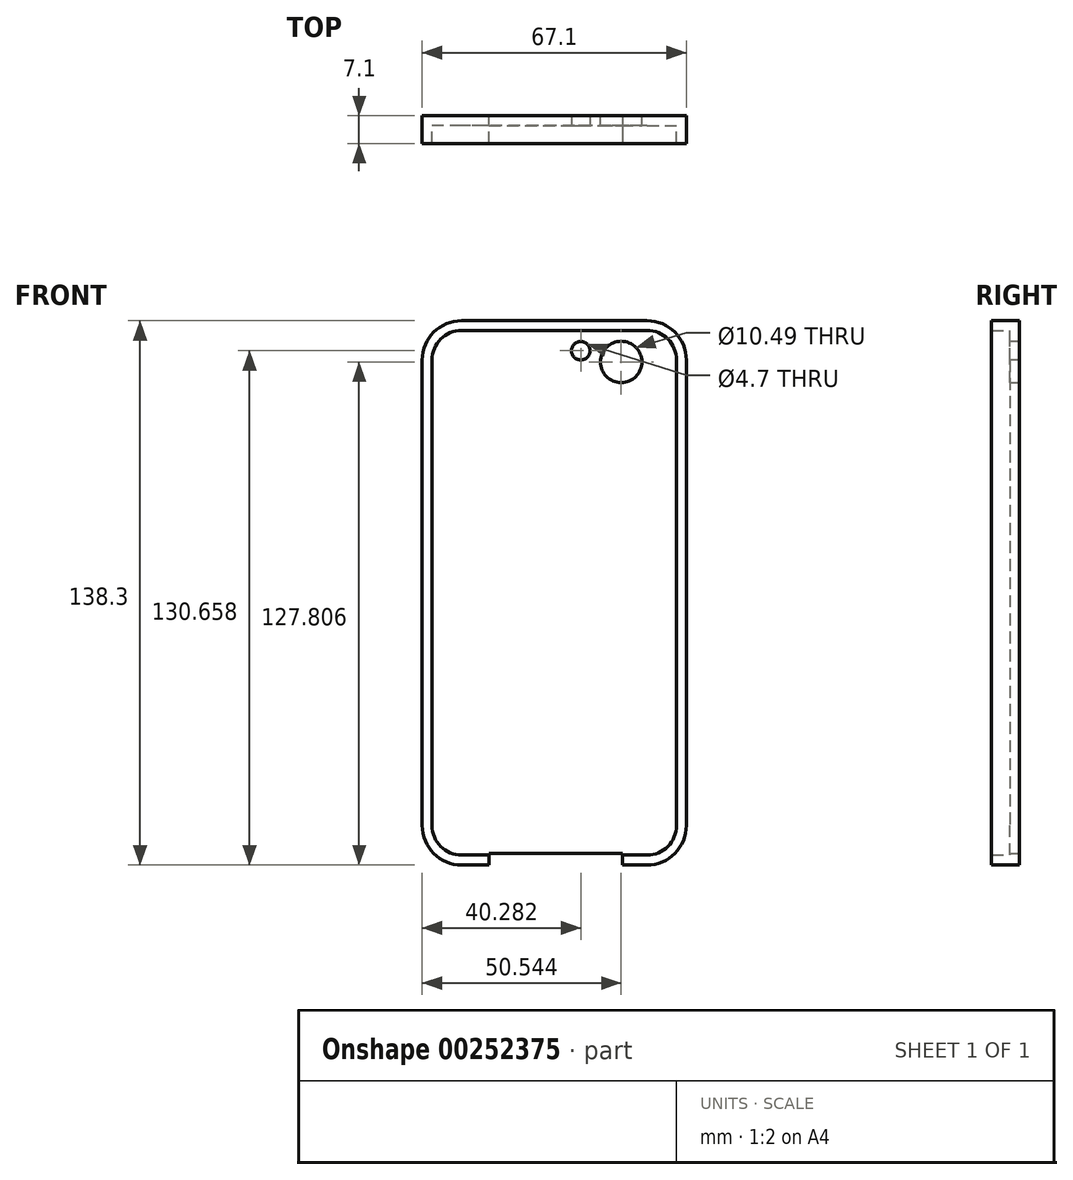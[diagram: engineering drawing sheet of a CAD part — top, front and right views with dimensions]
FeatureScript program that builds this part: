
annotation { "Feature Type Name" : "Feature", "Feature Type Description" : "" }
export const myFeature = defineFeature(function(context is Context, id is Id, definition is map)
    precondition{}
    {
        {
            var Q0;
            Q0=qCreatedBy(makeId("Front.planeOp"),FACE);
            var sketch = newSketch(context, id + "F0", { "sketchPlane" : qUnion([Q0])});
            skLineSegment(sketch, "E0.bottom", {"start": v(33.55, 69.15) * mm, "end": v(-33.55, 69.15) * mm});
            skLineSegment(sketch, "E0.top", {"start": v(33.55, -69.15) * mm, "end": v(-33.55, -69.15) * mm});
            skLineSegment(sketch, "E0.left", {"start": v(33.55, 69.15) * mm, "end": v(33.55, -69.15) * mm});
            skLineSegment(sketch, "E0.right", {"start": v(-33.55, 69.15) * mm, "end": v(-33.55, -69.15) * mm});
            skPoint(sketch, "E0.middle", {"position": v(0, 0) * mm});
            skSolve(sketch);
        }
        {
            var Q0;
            Q0=makeQuery(id+"F0.imprint","IMPRINT",FACE,{"disambiguationData":[TD([[makeQuery(id+"F0.imprint","IMPRINT",EDGE,{"derivedFrom":sQuery(id+"F0.wireOp",EDGE,"E0.bottom")}),1.0]])]});
            extrude(context, id + "F1", {"entities" : qUnion([Q0]), "endBound" : BoundingType.SYMMETRIC, "depth" : 7.1 * mm});
        }
        {
            var Q0;
            Q0=makeQuery(id+"F1.opExtrude","SWEPT_EDGE",EDGE,{"disambiguationData":[OSD([sQuery(id+"F0.wireOp",EDGE,"E0.top"),sQuery(id+"F0.wireOp",EDGE,"E0.left")])]});
            var Q1;
            Q1=makeQuery(id+"F1.opExtrude","SWEPT_EDGE",EDGE,{"disambiguationData":[OSD([sQuery(id+"F0.wireOp",EDGE,"E0.bottom"),sQuery(id+"F0.wireOp",EDGE,"E0.left")])]});
            var Q2;
            Q2=makeQuery(id+"F1.opExtrude","SWEPT_EDGE",EDGE,{"disambiguationData":[OSD([sQuery(id+"F0.wireOp",EDGE,"E0.top"),sQuery(id+"F0.wireOp",EDGE,"E0.right")])]});
            var Q3;
            Q3=makeQuery(id+"F1.opExtrude","SWEPT_EDGE",EDGE,{"disambiguationData":[OSD([sQuery(id+"F0.wireOp",EDGE,"E0.bottom"),sQuery(id+"F0.wireOp",EDGE,"E0.right")])]});
            fillet(context, id + "F2", {"entities" : qUnion([Q0, Q1, Q2, Q3]), "radius" : 10 * mm, "tangentPropagation" : true, "allowEdgeOverflow" : false});
        }
        {
            var Q0;
            Q0=makeQuery(id+"F1.opExtrude","CAP_FACE",FACE,{"disambiguationData":[OSD([sQuery(id+"F0.wireOp",EDGE,"E0.bottom"),sQuery(id+"F0.wireOp",EDGE,"E0.top"),sQuery(id+"F0.wireOp",EDGE,"E0.left"),sQuery(id+"F0.wireOp",EDGE,"E0.right")])],"isStart":false});
            shell(context, id + "F3", {"entities" : qUnion([Q0]), "thickness" : 2.5 * mm});
        }
        {
            var Q0;
            Q0=qCreatedBy(makeId("Front.planeOp"),FACE);
            var sketch = newSketch(context, id + "F4", { "sketchPlane" : qUnion([Q0])});
            skCircle(sketch, "E1", {"center": v(17, 58.66) * mm, "radius": 5.25 * mm});
            skSolve(sketch);
        }
        {
            var Q0;
            Q0 = qSketchRegion(id + "F4", true);
            extrude(context, id + "F5", {"entities" : qUnion([Q0]), "operationType" : NewBodyOperationType.REMOVE, "endBound" : BoundingType.SYMMETRIC, "depth" : 25 * mm});
        }
        {
            var Q0;
            Q0=makeQuery(id+"F1.opExtrude","SWEPT_FACE",FACE,{"disambiguationData":[OSD([sQuery(id+"F0.wireOp",EDGE,"E0.top")])]});
            var sketch = newSketch(context, id + "F6", { "sketchPlane" : qUnion([Q0])});
            skLineSegment(sketch, "E2", {"start": v(-16.64, 3.55) * mm, "end": v(-16.64, -3.55) * mm});
            skLineSegment(sketch, "E3", {"start": v(-16.64, -3.55) * mm, "end": v(17.35, -3.55) * mm});
            skLineSegment(sketch, "E4", {"start": v(17.35, -3.55) * mm, "end": v(17.35, 3.55) * mm});
            skLineSegment(sketch, "E5", {"start": v(17.35, 3.55) * mm, "end": v(-16.64, 3.55) * mm});
            skSolve(sketch);
        }
        {
            var Q0;
            Q0=makeQuery(id+"F6.imprint","IMPRINT",FACE,{"disambiguationData":[TD([[makeQuery(id+"F6.imprint","IMPRINT",EDGE,{"derivedFrom":sQuery(id+"F6.wireOp",EDGE,"E2")}),1.0]])]});
            extrude(context, id + "F7", {"entities" : qUnion([Q0]), "operationType" : NewBodyOperationType.REMOVE, "endBound" : BoundingType.SYMMETRIC, "oppositeDirection" : true, "depth" : 6 * mm});
        }
        {
            var Q0;
            Q0=qCreatedBy(makeId("Front.planeOp"),FACE);
            var sketch = newSketch(context, id + "F8", { "sketchPlane" : qUnion([Q0])});
            skCircle(sketch, "E6", {"center": v(6.73, 61.5) * mm, "radius": 2.35 * mm});
            skSolve(sketch);
        }
        {
            var Q0;
            Q0 = qSketchRegion(id + "F8", true);
            extrude(context, id + "F9", {"entities" : qUnion([Q0]), "operationType" : NewBodyOperationType.REMOVE, "endBound" : BoundingType.SYMMETRIC, "oppositeDirection" : true, "depth" : 25 * mm});
        }
    });
